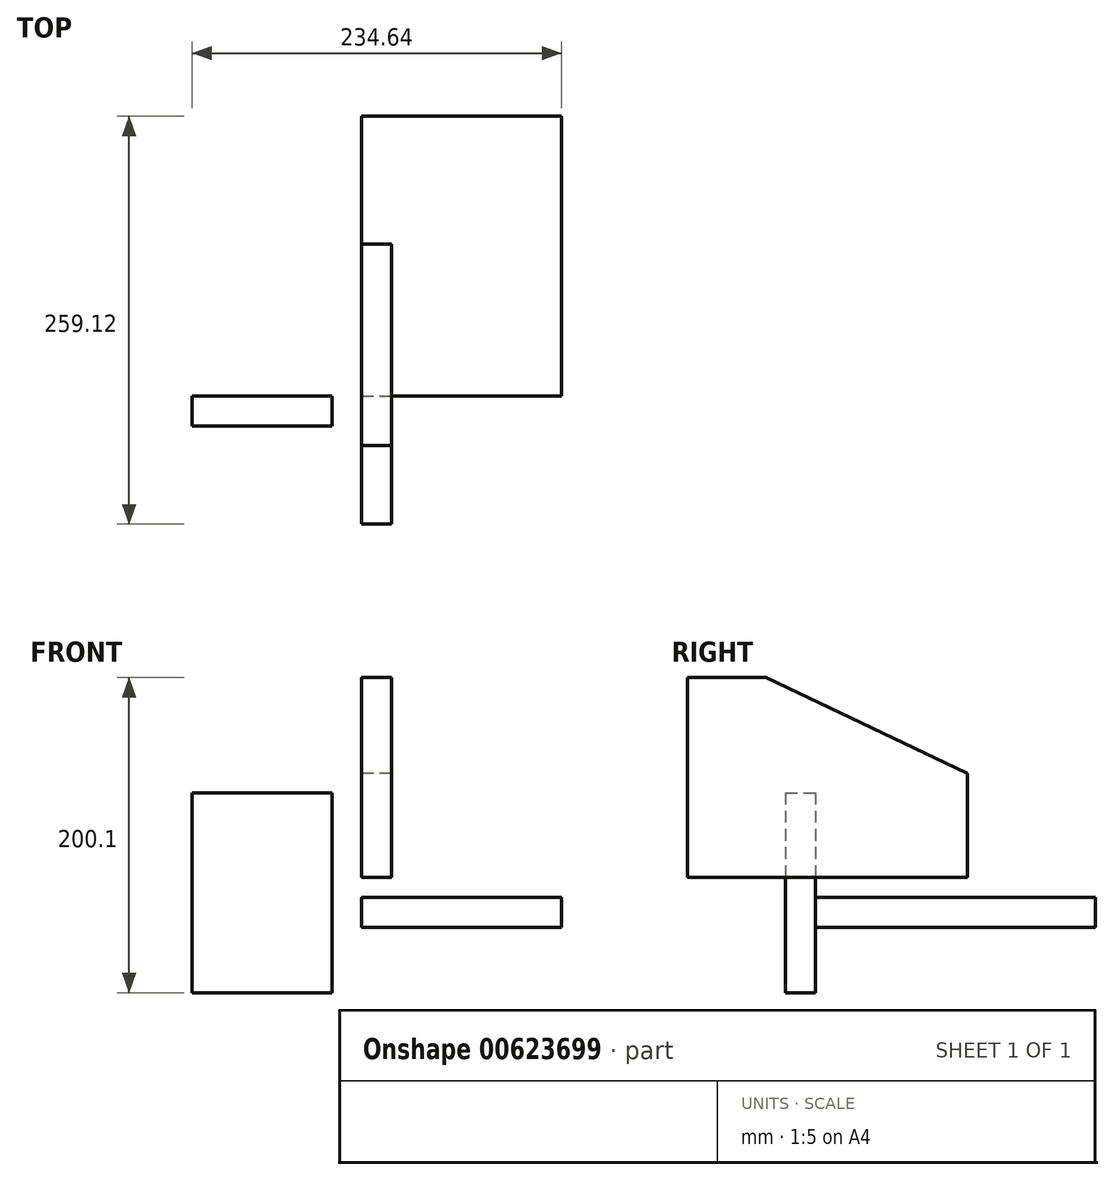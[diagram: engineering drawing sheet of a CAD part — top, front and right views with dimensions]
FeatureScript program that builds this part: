
annotation { "Feature Type Name" : "Feature", "Feature Type Description" : "" }
export const myFeature = defineFeature(function(context is Context, id is Id, definition is map)
    precondition{}
    {
        {
            var Q0;
            Q0=qCreatedBy(makeId("Top.planeOp"),FACE);
            var sketch = newSketch(context, id + "F0", { "sketchPlane" : qUnion([Q0])});
            skLineSegment(sketch, "E0.bottom", {"start": v(0, 0) * mm, "end": v(127, 0) * mm});
            skLineSegment(sketch, "E0.top", {"start": v(0, 177.8) * mm, "end": v(127, 177.8) * mm});
            skLineSegment(sketch, "E0.left", {"start": v(0, 0) * mm, "end": v(0, 177.8) * mm});
            skLineSegment(sketch, "E0.right", {"start": v(127, 0) * mm, "end": v(127, 177.8) * mm});
            skSolve(sketch);
        }
        {
            var Q0;
            Q0=makeQuery(id+"F0.imprint","IMPRINT",FACE,{"disambiguationData":[TD([[makeQuery(id+"F0.imprint","IMPRINT",EDGE,{"derivedFrom":sQuery(id+"F0.wireOp",EDGE,"E0.bottom")}),1.0]])]});
            extrude(context, id + "F1", {"entities" : qUnion([Q0]), "depth" : 19.05 * mm, "offsetDistance" : 25.4 * mm});
        }
        {
            var Q0;
            Q0=qCreatedBy(makeId("Right.planeOp"),FACE);
            var sketch = newSketch(context, id + "F2", { "sketchPlane" : qUnion([Q0])});
            skLineSegment(sketch, "E1.bottom", {"start": v(96.48, 31.74) * mm, "end": v(-81.32, 31.74) * mm});
            skLineSegment(sketch, "E1.top", {"start": v(96.48, 158.74) * mm, "end": v(-81.32, 158.74) * mm});
            skLineSegment(sketch, "E1.left", {"start": v(96.48, 31.74) * mm, "end": v(96.48, 158.74) * mm});
            skLineSegment(sketch, "E1.right", {"start": v(-81.32, 31.74) * mm, "end": v(-81.32, 158.74) * mm});
            skSolve(sketch);
        }
        {
            var Q0;
            Q0=makeQuery(id+"F2.imprint","IMPRINT",FACE,{"disambiguationData":[TD([[makeQuery(id+"F2.imprint","IMPRINT",EDGE,{"derivedFrom":sQuery(id+"F2.wireOp",EDGE,"E1.bottom")}),-1.0]])]});
            extrude(context, id + "F3", {"entities" : qUnion([Q0]), "depth" : 19.05 * mm, "offsetDistance" : 25.4 * mm});
        }
        {
            var Q0;
            Q0=makeQuery(id+"F3.opExtrude","CAP_FACE",FACE,{"disambiguationData":[OSD([sQuery(id+"F2.wireOp",EDGE,"E1.bottom"),sQuery(id+"F2.wireOp",EDGE,"E1.top"),sQuery(id+"F2.wireOp",EDGE,"E1.left"),sQuery(id+"F2.wireOp",EDGE,"E1.right")])],"isStart":true});
            var sketch = newSketch(context, id + "F4", { "sketchPlane" : qUnion([Q0])});
            skLineSegment(sketch, "E2", {"start": v(31.48, 158.74) * mm, "end": v(-96.48, 97.97) * mm});
            skSolve(sketch);
        }
        {
            var Q0;
            {var subQ0=sQuery(id+"F4.wireOp",EDGE,"E2");Q0=makeQuery(id+"F4.imprint","IMPRINT",FACE,{"disambiguationData":[TD([[makeQuery(id+"F4.imprint","IMPRINT",EDGE,{"derivedFrom":subQ0}),-1.0]])]});}
            extrude(context, id + "F5", {"entities" : qUnion([Q0]), "operationType" : NewBodyOperationType.REMOVE, "endBound" : BoundingType.THROUGH_ALL, "oppositeDirection" : true, "depth" : 25.4 * mm, "offsetDistance" : 25.4 * mm});
        }
        {
            var Q0;
            Q0=qCreatedBy(makeId("Front.planeOp"),FACE);
            var sketch = newSketch(context, id + "F6", { "sketchPlane" : qUnion([Q0])});
            skLineSegment(sketch, "E3.bottom", {"start": v(-107.64, 85.64) * mm, "end": v(-18.74, 85.64) * mm});
            skLineSegment(sketch, "E3.top", {"start": v(-107.64, -41.36) * mm, "end": v(-18.74, -41.36) * mm});
            skLineSegment(sketch, "E3.left", {"start": v(-107.64, 85.64) * mm, "end": v(-107.64, -41.36) * mm});
            skLineSegment(sketch, "E3.right", {"start": v(-18.74, 85.64) * mm, "end": v(-18.74, -41.36) * mm});
            skSolve(sketch);
        }
        {
            var Q0;
            Q0=makeQuery(id+"F6.imprint","IMPRINT",FACE,{"disambiguationData":[TD([[makeQuery(id+"F6.imprint","IMPRINT",EDGE,{"derivedFrom":sQuery(id+"F6.wireOp",EDGE,"E3.bottom")}),-1.0]])]});
            extrude(context, id + "F7", {"entities" : qUnion([Q0]), "depth" : 19.05 * mm, "offsetDistance" : 25.4 * mm});
        }
    });
